# Revit family: Ladder_FoldDown_KattsafeUSA_Commercial
name_source: partatom
category: Specialty Equipment
units: mm (PartAtom-declared; Revit-internal decimal feet)

## family parameters
Always vertical = Yes
Classification Number = 23.17.23.15
Cut with Voids When Loaded = Yes
Enable Cutting in Views = No
Maintain Annotation Orientation = No
Part Type = Normal
Room Calculation Point = No
Round Connector Dimension = Use Diameter
Shared = No
Work Plane-Based = No

## types (1)
- RL62
    Assembly Code = E1090100
    Default Elevation = 0' - 0"
    Description = The RL62 model is perfect for reaching heights between 7 and 10 ft. This small-but-mighty ladder installs easily and provides 1 ¼-inch serrated rungs that we’ve robotically welded to the stiles. Plus, it folds up into a compact 33 ½-inch by 51-inch opening, giving you additional floor space.
    ElementType = Ladder
    Export Type to IFC As = IfcBuildingElementProxy
    IfcExportAs = IfcBuildingElementProxy
    IfcExportType = USERDEFINED
    Manufacturer = Kattsafe®
    ManufacturerOverallDepth = 2' - 9 1/2"
    ManufacturerOverallWidth = 4' - 3"
    ManufacturerSpecCode = RL62
    ManufacturerURLProductSpecific = https://kattsafe.com
    Material = Aluminum_Kattsafe_Satin
    Model = RL62
    ModifiedIssue = 20250703 $
    Type Comments = Ladder - Commercial - Fold Down
    Type IFC Predefined Type = USERDEFINED
    URL = https://kattsafe.com
    Uniclass2015Code = Pr_25_30_85_02
    Uniclass2015Title = Access ladders
    Uniclass2015Version = Products v1.35

## geometry (parser evidence)
native form markers: Sweep x5
no freeform markers — native parametric forms only
